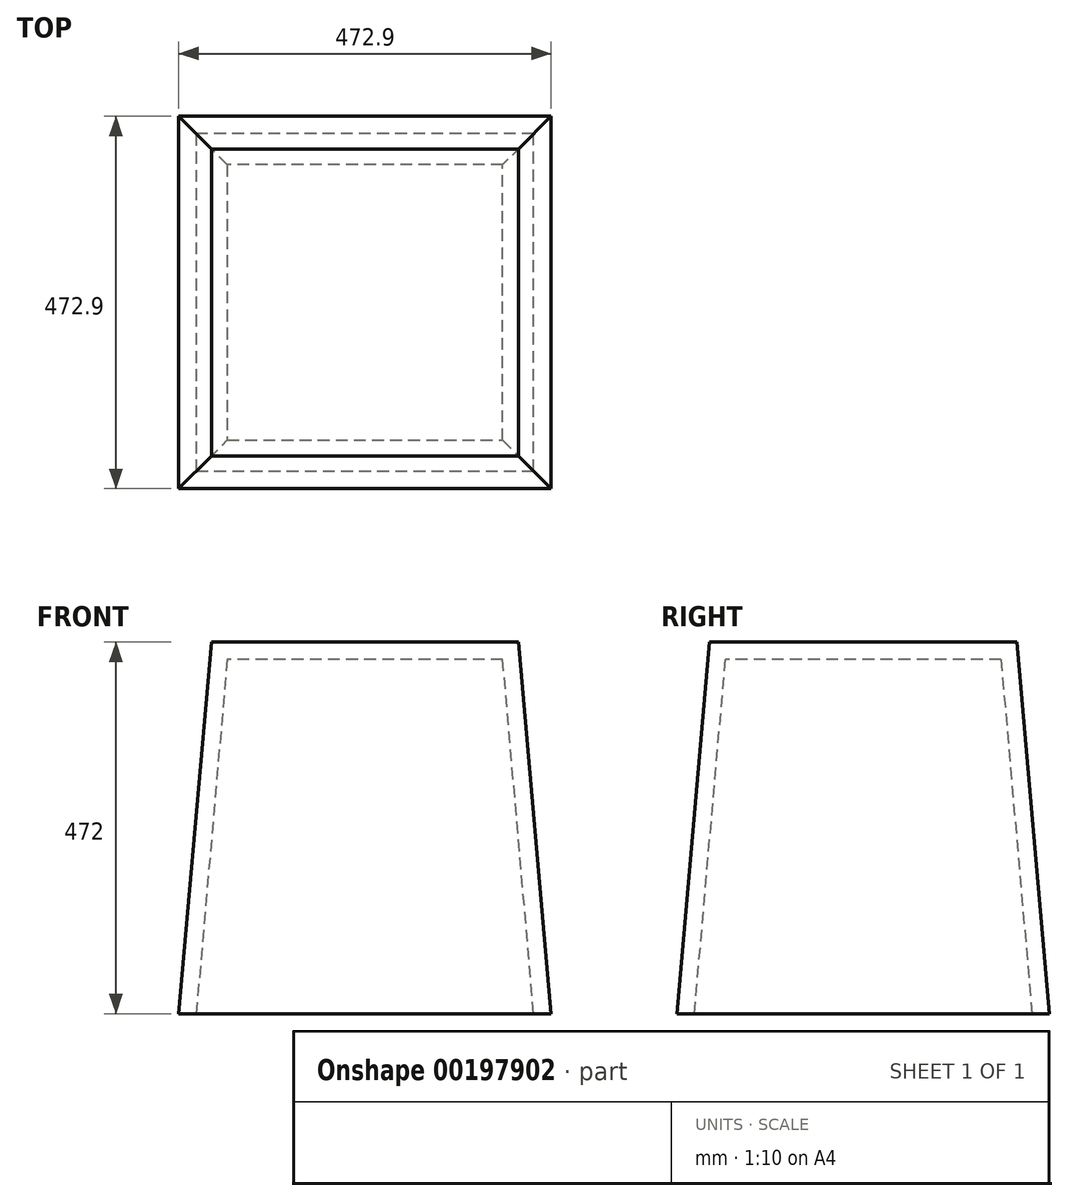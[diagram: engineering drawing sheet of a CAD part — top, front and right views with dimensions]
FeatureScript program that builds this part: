
annotation { "Feature Type Name" : "Feature", "Feature Type Description" : "" }
export const myFeature = defineFeature(function(context is Context, id is Id, definition is map)
    precondition{}
    {
        {
            var Q0;
            Q0=qCreatedBy(makeId("Top.planeOp"),FACE);
            var sketch = newSketch(context, id + "F0", { "sketchPlane" : qUnion([Q0])});
            skLineSegment(sketch, "E0", {"start": v(0, 264.04) * mm, "end": v(0, -236.88) * mm, "construction": true});
            skLineSegment(sketch, "E1", {"start": v(-259.8, 0) * mm, "end": v(230.93, 0) * mm, "construction": true});
            skLineSegment(sketch, "E2.bottom", {"start": v(-175, 175) * mm, "end": v(175, 175) * mm});
            skLineSegment(sketch, "E2.top", {"start": v(-175, -175) * mm, "end": v(175, -175) * mm});
            skLineSegment(sketch, "E2.left", {"start": v(-175, 175) * mm, "end": v(-175, -175) * mm});
            skLineSegment(sketch, "E2.right", {"start": v(175, 175) * mm, "end": v(175, -175) * mm});
            skSolve(sketch);
        }
        {
            var Q0;
            Q0 = qSketchRegion(id + "F0", true);
            extrude(context, id + "F1", {"entities" : qUnion([Q0]), "oppositeDirection" : true, "depth" : 450 * mm, "hasDraft" : true, "draftAngle" : 5 * degree});
        }
        {
            var Q0;
            Q0=makeQuery(id+"F1.opExtrude","CAP_FACE",FACE,{"disambiguationData":[OSD([sQuery(id+"F0.wireOp",EDGE,"E2.bottom"),sQuery(id+"F0.wireOp",EDGE,"E2.top"),sQuery(id+"F0.wireOp",EDGE,"E2.left"),sQuery(id+"F0.wireOp",EDGE,"E2.right")])],"isStart":false});
            shell(context, id + "F2", {"entities" : qUnion([Q0]), "thickness" : 22 * mm, "oppositeDirection" : true});
        }
    });
